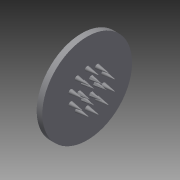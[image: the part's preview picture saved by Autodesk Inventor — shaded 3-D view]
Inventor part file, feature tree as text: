
AUTODESK INVENTOR PART (.ipt)
format: ipt  version: 2015 (Build 190159000, 159)  size: 174,592 bytes
history: native  units: in
note: dims shown in document units (in); Inventor stores cm internally (conversion verified against a paired STEP export)
features: extrude x5, sketch x5, pattern_circular x2
ambient origin geometry x8: Origin, YZ Plane, XZ Plane, XY Plane, X Axis, Y Axis, Z Axis, Center Point
bodies: Solid1 (feature_tree)
feature tree (12):
  extrude  "Extrusion1"  Depth=0.125in TaperAngle=0.0deg
  extrude  "Extrusion2"  Depth=0.5in
  pattern_circular  "Circular Pattern1"  Count=10 Angle=360.0deg
  extrude  "Extrusion3"  Depth=0.5in TaperAngle=360.0deg
  pattern_circular  "Circular Pattern2"  [2 undecoded]
  extrude  "Extrusion4"  Depth=0.125in TaperAngle=0.0deg
  extrude  "Extrusion5"  [1 undecoded]
  sketch  "Sketch1"  dims[d0=4.0in d1=0.125in d2=0.0in]
  sketch  "Sketch2"  dims[d3=0.2in d4=0.5in d5=-0.0687in d6=3.937in d7=360.0deg]
  sketch  "Sketch3"  dims[d9=0.5in d10=-0.0687in d11=2.3622in d12=360.0deg]
  sketch  "Sketch4"  dims[d14=0.43in]
  sketch  "Sketch5"  dims[d15=0.125in d16=0.0in d17=0.25in d18=0.125in d19=0.0in]
note: 3 required parameter values undecoded (feature->parameter linkage not recoverable at this tier; creation-order binding heuristic only, values carry confidence <= 0.55)
